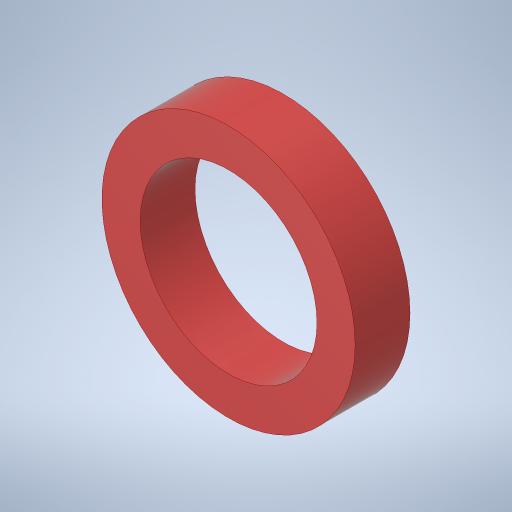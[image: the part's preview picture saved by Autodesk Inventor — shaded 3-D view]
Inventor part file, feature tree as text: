
AUTODESK INVENTOR PART (.ipt)
format: ipt  version: 2023.4 (Build 274418000, 418)  size: 246,784 bytes
history: native  units: in
note: dims shown in document units (in); Inventor stores cm internally (conversion verified against a paired STEP export)
features: extrude x1
ambient origin geometry x8: Origin, YZ Plane, XZ Plane, XY Plane, X Axis, Y Axis, Z Axis, Center Point
bodies: Solid1 (feature_tree)
feature tree (1):
  extrude  "Extrusion1"  TaperAngle=0.0deg  [1 undecoded]
note: 1 required parameter value undecoded (feature->parameter linkage not recoverable at this tier; creation-order binding heuristic only, values carry confidence <= 0.55)
